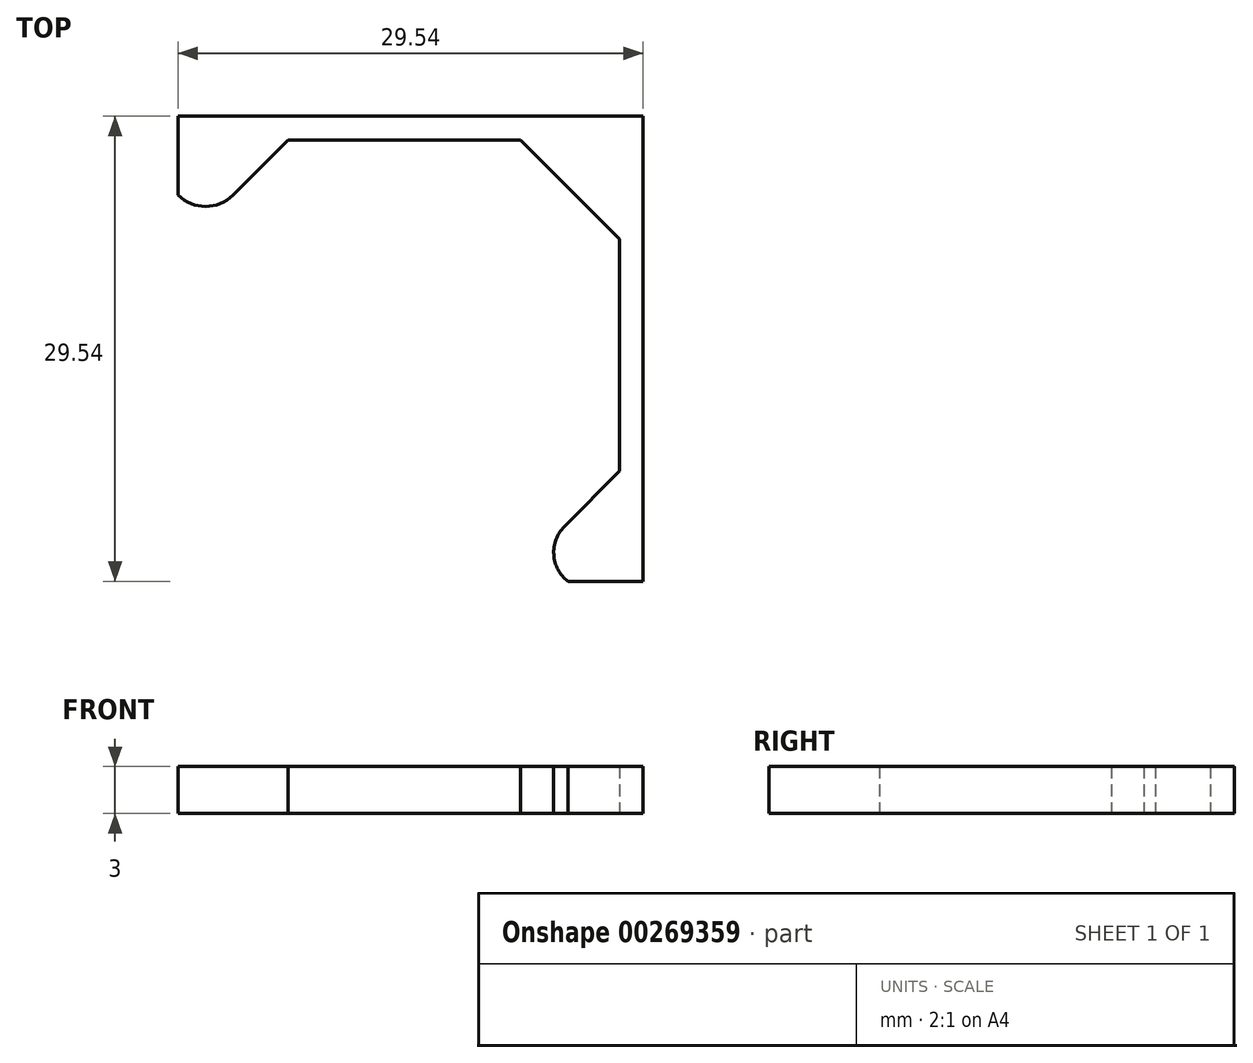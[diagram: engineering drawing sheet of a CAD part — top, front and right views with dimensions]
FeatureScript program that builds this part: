
annotation { "Feature Type Name" : "Feature", "Feature Type Description" : "" }
export const myFeature = defineFeature(function(context is Context, id is Id, definition is map)
    precondition{}
    {
        {
            var Q0;
            Q0=qCreatedBy(makeId("Top.planeOp"),FACE);
            var sketch = newSketch(context, id + "F0", { "sketchPlane" : qUnion([Q0])});
            skPoint(sketch, "E0.middle", {"position": v(0, 0) * mm});
            skLineSegment(sketch, "E1", {"start": v(-0.63, 15) * mm, "end": v(-8, 15) * mm});
            skLineSegment(sketch, "E2", {"start": v(-8, 15) * mm, "end": v(-0.63, 15) * mm});
            skLineSegment(sketch, "E3", {"start": v(6.75, 15) * mm, "end": v(-0.63, 15) * mm});
            skLineSegment(sketch, "E4", {"start": v(13.04, 1.33) * mm, "end": v(13.04, 8.7) * mm});
            skLineSegment(sketch, "E5", {"start": v(13.04, 8.7) * mm, "end": v(13.04, 1.33) * mm});
            skLineSegment(sketch, "E6", {"start": v(13.04, -6.04) * mm, "end": v(13.04, 1.33) * mm});
            skLineSegment(sketch, "E7", {"start": v(6.75, 15) * mm, "end": v(13.04, 8.7) * mm});
            skLineSegment(sketch, "E8", {"start": v(9.54, -9.54) * mm, "end": v(13.04, -6.04) * mm});
            skLineSegment(sketch, "E9", {"start": v(-11.5, 11.5) * mm, "end": v(-8, 15) * mm});
            skArc(sketch, "E10", {"start": v(-11.5, 11.5) * mm, "mid": v(-13.25, 10.78) * mm, "end": v(-15, 11.5) * mm});
            skArc(sketch, "E11", {"start": v(9.54, -9.54) * mm, "mid": v(8.86, -11.35) * mm, "end": v(9.77, -13.04) * mm});
            skLineSegment(sketch, "E12", {"start": v(-15, 16.5) * mm, "end": v(14.54, 16.5) * mm});
            skLineSegment(sketch, "E13", {"start": v(-15, 16.5) * mm, "end": v(-15, 11.5) * mm});
            skLineSegment(sketch, "E14", {"start": v(9.77, -13.04) * mm, "end": v(14.54, -13.04) * mm});
            skLineSegment(sketch, "E15", {"start": v(14.54, -13.04) * mm, "end": v(14.54, 16.5) * mm});
            skSolve(sketch);
        }
        {
            var Q0;
            Q0 = qSketchRegion(id + "F0", true);
            extrude(context, id + "F1", {"entities" : qUnion([Q0]), "depth" : 3 * mm});
        }
    });
